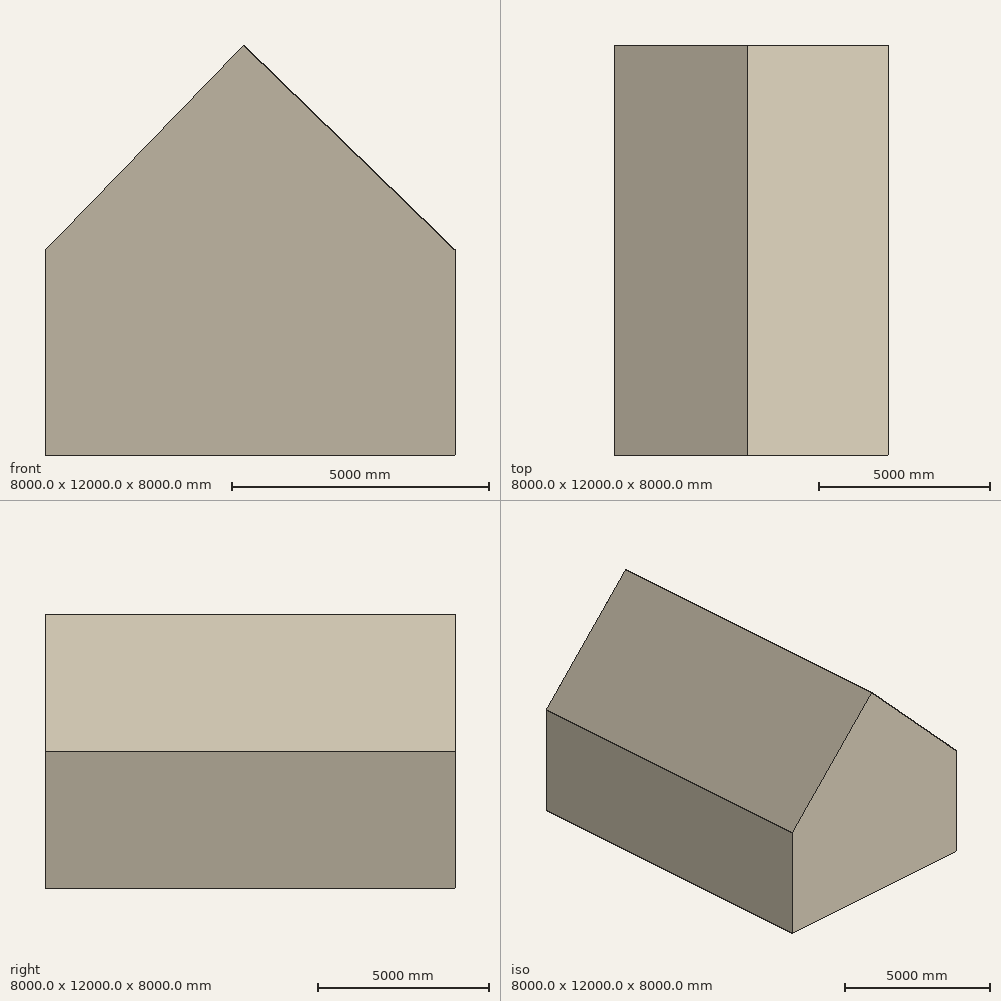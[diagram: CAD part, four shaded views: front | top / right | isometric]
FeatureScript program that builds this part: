
annotation { "Feature Type Name" : "Feature", "Feature Type Description" : "" }
export const myFeature = defineFeature(function(context is Context, id is Id, definition is map)
    precondition{}
    {
        {
            var Q0;
            Q0=qCreatedBy(makeId("Front.planeOp"),FACE);
            var sketch = newSketch(context, id + "F0", { "sketchPlane" : qUnion([Q0])});
            skLineSegment(sketch, "E0", {"start": v(8000, 0) * mm, "end": v(8000, -4000) * mm});
            skLineSegment(sketch, "E1", {"start": v(8000, -4000) * mm, "end": v(0, -4000) * mm});
            skLineSegment(sketch, "E2", {"start": v(0, -4000) * mm, "end": v(0, 0) * mm});
            skLineSegment(sketch, "E3", {"start": v(0, 0) * mm, "end": v(3870.69, 4000) * mm});
            skLineSegment(sketch, "E4", {"start": v(3870.69, 4000) * mm, "end": v(8000, 0) * mm});
            skSolve(sketch);
        }
        {
            var Q0;
            Q0 = qSketchRegion(id + "F0", true);
            extrude(context, id + "F1", {"entities" : qUnion([Q0]), "depth" : 12000 * mm});
        }
    });
